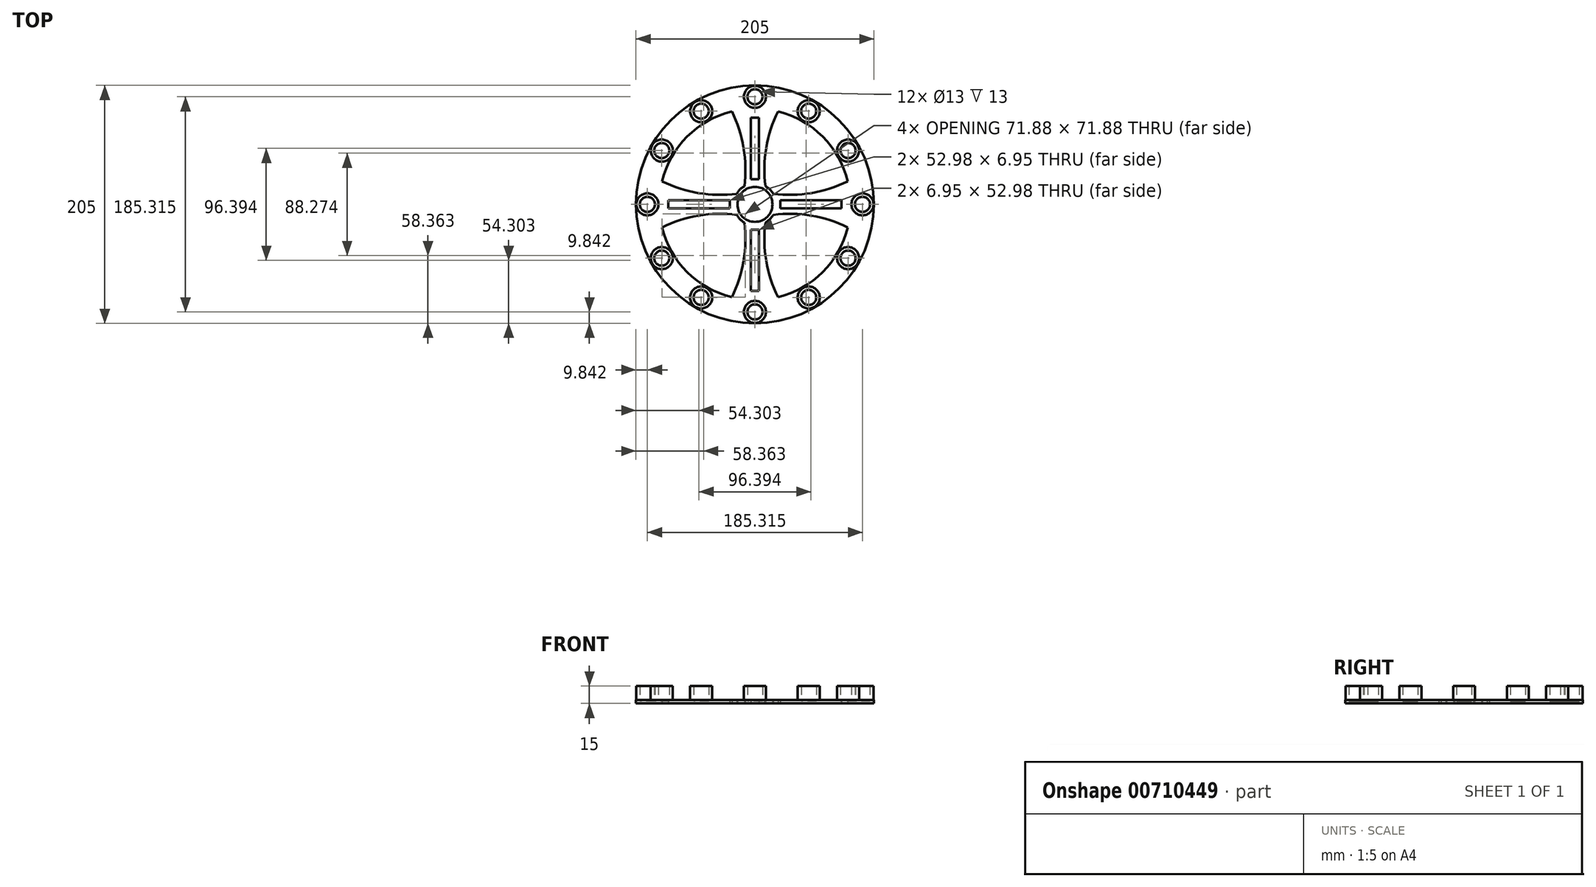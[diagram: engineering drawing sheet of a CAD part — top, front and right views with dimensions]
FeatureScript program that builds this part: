
annotation { "Feature Type Name" : "Feature", "Feature Type Description" : "" }
export const myFeature = defineFeature(function(context is Context, id is Id, definition is map)
    precondition{}
    {
        {
            var Q0;
            Q0=qCreatedBy(makeId("Top.planeOp"),FACE);
            var sketch = newSketch(context, id + "F0", { "sketchPlane" : qUnion([Q0])});
            skCircle(sketch, "E0", {"center": v(0, 0) * mm, "radius": 82.5 * mm});
            skCircle(sketch, "E1.0", {"center": v(0, 0) * mm, "radius": 102.5 * mm});
            skCircle(sketch, "E2", {"center": v(0, 92.66) * mm, "radius": 6.5 * mm});
            skCircle(sketch, "E3.0", {"center": v(0, 92.66) * mm, "radius": 9.5 * mm});
            skCircle(sketch, "E4.1.0", {"center": v(-46.33, 80.24) * mm, "radius": 9.5 * mm});
            skCircle(sketch, "E4.1.1", {"center": v(-46.33, 80.24) * mm, "radius": 6.5 * mm});
            skCircle(sketch, "E4.2.0", {"center": v(-80.24, 46.33) * mm, "radius": 9.5 * mm});
            skCircle(sketch, "E4.2.1", {"center": v(-80.24, 46.33) * mm, "radius": 6.5 * mm});
            skCircle(sketch, "E4.3.0", {"center": v(-92.66, 0) * mm, "radius": 9.5 * mm});
            skCircle(sketch, "E4.3.1", {"center": v(-92.66, 0) * mm, "radius": 6.5 * mm});
            skCircle(sketch, "E4.4.0", {"center": v(-80.24, -46.33) * mm, "radius": 9.5 * mm});
            skCircle(sketch, "E4.4.1", {"center": v(-80.24, -46.33) * mm, "radius": 6.5 * mm});
            skCircle(sketch, "E4.5.0", {"center": v(-46.33, -80.24) * mm, "radius": 9.5 * mm});
            skCircle(sketch, "E4.5.1", {"center": v(-46.33, -80.24) * mm, "radius": 6.5 * mm});
            skCircle(sketch, "E4.6.0", {"center": v(0, -92.66) * mm, "radius": 9.5 * mm});
            skCircle(sketch, "E4.6.1", {"center": v(0, -92.66) * mm, "radius": 6.5 * mm});
            skCircle(sketch, "E4.7.0", {"center": v(46.33, -80.24) * mm, "radius": 9.5 * mm});
            skCircle(sketch, "E4.7.1", {"center": v(46.33, -80.24) * mm, "radius": 6.5 * mm});
            skCircle(sketch, "E4.8.0", {"center": v(80.24, -46.33) * mm, "radius": 9.5 * mm});
            skCircle(sketch, "E4.8.1", {"center": v(80.24, -46.33) * mm, "radius": 6.5 * mm});
            skCircle(sketch, "E4.9.0", {"center": v(92.66, 0) * mm, "radius": 9.5 * mm});
            skCircle(sketch, "E4.9.1", {"center": v(92.66, 0) * mm, "radius": 6.5 * mm});
            skCircle(sketch, "E5.1.10.0", {"center": v(80.24, 46.33) * mm, "radius": 9.5 * mm});
            skCircle(sketch, "E5.2.10.0", {"center": v(80.24, 46.33) * mm, "radius": 6.5 * mm});
            skCircle(sketch, "E5.1.11.0", {"center": v(46.33, 80.24) * mm, "radius": 9.5 * mm});
            skCircle(sketch, "E5.2.11.0", {"center": v(46.33, 80.24) * mm, "radius": 6.5 * mm});
            skLineSegment(sketch, "E6.MirrorCS", {"start": v(-74.04, -3.28) * mm, "end": v(-74.04, 3.35) * mm});
            skArc(sketch, "E7", {"start": v(-80.07, 19.86) * mm, "mid": v(-46.62, 9.4) * mm, "end": v(-11.57, 9.7) * mm});
            skArc(sketch, "E8.1.0", {"start": v(-19.86, -80.07) * mm, "mid": v(-9.4, -46.62) * mm, "end": v(-9.7, -11.57) * mm});
            skArc(sketch, "E8.2.0", {"start": v(80.07, -19.86) * mm, "mid": v(46.62, -9.4) * mm, "end": v(11.57, -9.7) * mm});
            skArc(sketch, "E8.3.0", {"start": v(19.86, 80.07) * mm, "mid": v(9.4, 46.62) * mm, "end": v(9.7, 11.57) * mm});
            skArc(sketch, "E9.MirrorCS", {"start": v(-80.07, -19.86) * mm, "mid": v(-46.62, -9.4) * mm, "end": v(-11.57, -9.7) * mm});
            skArc(sketch, "E10.MirrorCS", {"start": v(19.86, -80.07) * mm, "mid": v(9.4, -46.62) * mm, "end": v(9.7, -11.57) * mm});
            skArc(sketch, "E11.MirrorCS", {"start": v(-19.86, 80.07) * mm, "mid": v(-9.4, 46.62) * mm, "end": v(-9.7, 11.57) * mm});
            skArc(sketch, "E12.MirrorCS", {"start": v(80.07, 19.86) * mm, "mid": v(46.62, 9.4) * mm, "end": v(11.57, 9.7) * mm});
            skLineSegment(sketch, "E13.bottom", {"start": v(-3.47, 74.69) * mm, "end": v(3.47, 74.69) * mm});
            skLineSegment(sketch, "E13.top", {"start": v(-3.47, 21.7) * mm, "end": v(3.47, 21.7) * mm});
            skLineSegment(sketch, "E13.left", {"start": v(-3.47, 74.69) * mm, "end": v(-3.47, 21.7) * mm});
            skLineSegment(sketch, "E13.right", {"start": v(3.47, 74.69) * mm, "end": v(3.47, 21.7) * mm});
            skPoint(sketch, "E13.middle", {"position": v(0, 48.2) * mm});
            skLineSegment(sketch, "E14.1.0", {"start": v(-74.69, 3.47) * mm, "end": v(-21.7, 3.47) * mm});
            skLineSegment(sketch, "E14.1.1", {"start": v(-74.69, -3.47) * mm, "end": v(-21.7, -3.47) * mm});
            skLineSegment(sketch, "E14.1.2", {"start": v(-74.69, -3.47) * mm, "end": v(-74.69, 3.47) * mm});
            skLineSegment(sketch, "E14.1.3", {"start": v(-21.7, -3.47) * mm, "end": v(-21.7, 3.47) * mm});
            skLineSegment(sketch, "E14.2.0", {"start": v(-3.47, -74.69) * mm, "end": v(-3.47, -21.7) * mm});
            skLineSegment(sketch, "E14.2.1", {"start": v(3.47, -74.69) * mm, "end": v(3.47, -21.7) * mm});
            skLineSegment(sketch, "E14.2.2", {"start": v(3.47, -74.69) * mm, "end": v(-3.47, -74.69) * mm});
            skLineSegment(sketch, "E14.2.3", {"start": v(3.47, -21.7) * mm, "end": v(-3.47, -21.7) * mm});
            skLineSegment(sketch, "E14.3.0", {"start": v(74.69, -3.47) * mm, "end": v(21.7, -3.47) * mm});
            skLineSegment(sketch, "E14.3.1", {"start": v(74.69, 3.47) * mm, "end": v(21.7, 3.47) * mm});
            skLineSegment(sketch, "E14.3.2", {"start": v(74.69, 3.47) * mm, "end": v(74.69, -3.47) * mm});
            skLineSegment(sketch, "E14.3.3", {"start": v(21.7, 3.47) * mm, "end": v(21.7, -3.47) * mm});
            skCircle(sketch, "E15", {"center": v(0, 0) * mm, "radius": 18.16 * mm});
            skCircle(sketch, "E16", {"center": v(0, 0) * mm, "radius": 15.1 * mm});
            skSolve(sketch);
        }
        {
            var Q0;
            Q0 = qSketchRegion(id + "F0", true);
            var Q1;
            Q1=makeQuery(id+"F0.imprint","IMPRINT",FACE,{"disambiguationData":[TD([[makeQuery(id+"F0.imprint","IMPRINT",EDGE,{"derivedFrom":sQuery(id+"F0.wireOp",EDGE,"E14.1.0")}),1.0]])]});
            var Q2;
            {var subQ0=sQuery(id+"F0.wireOp",EDGE,"E16");var subQ1=sQuery(id+"F0.wireOp",EDGE,"E7");var subQ2=makeQuery(id+"F0.imprint","INTERSECT",VERTEX,{"derivedFrom":[subQ1,subQ0]});Q2=makeQuery(id+"F0.imprint","IMPRINT",FACE,{"disambiguationData":[TD([[makeQuery(id+"F0.imprint","IMPRINT",EDGE,{"disambiguationData":[TD([[subQ2,1.0]])],"derivedFrom":subQ1}),-1.0]])]});}
            var Q3;
            {var subQ0=sQuery(id+"F0.wireOp",EDGE,"E16");var subQ1=sQuery(id+"F0.wireOp",EDGE,"E7");var subQ2=makeQuery(id+"F0.imprint","INTERSECT",VERTEX,{"derivedFrom":[subQ1,subQ0]});Q3=makeQuery(id+"F0.imprint","IMPRINT",FACE,{"disambiguationData":[TD([[makeQuery(id+"F0.imprint","IMPRINT",EDGE,{"disambiguationData":[TD([[subQ2,1.0]])],"derivedFrom":subQ1}),1.0]])]});}
            var Q4;
            {var subQ0=sQuery(id+"F0.wireOp",EDGE,"E16");var subQ1=sQuery(id+"F0.wireOp",EDGE,"E8.3.0");var subQ2=makeQuery(id+"F0.imprint","INTERSECT",VERTEX,{"derivedFrom":[subQ1,subQ0]});Q4=makeQuery(id+"F0.imprint","IMPRINT",FACE,{"disambiguationData":[TD([[makeQuery(id+"F0.imprint","IMPRINT",EDGE,{"disambiguationData":[TD([[subQ2,1.0]])],"derivedFrom":subQ1}),-1.0]])]});}
            var Q5;
            {var subQ0=sQuery(id+"F0.wireOp",EDGE,"E16");var subQ1=sQuery(id+"F0.wireOp",EDGE,"E8.3.0");var subQ2=makeQuery(id+"F0.imprint","INTERSECT",VERTEX,{"derivedFrom":[subQ1,subQ0]});Q5=makeQuery(id+"F0.imprint","IMPRINT",FACE,{"disambiguationData":[TD([[makeQuery(id+"F0.imprint","IMPRINT",EDGE,{"disambiguationData":[TD([[subQ2,1.0]])],"derivedFrom":subQ1}),1.0]])]});}
            var Q6;
            {var subQ0=sQuery(id+"F0.wireOp",EDGE,"E16");var subQ1=sQuery(id+"F0.wireOp",EDGE,"E8.2.0");var subQ2=makeQuery(id+"F0.imprint","INTERSECT",VERTEX,{"derivedFrom":[subQ1,subQ0]});Q6=makeQuery(id+"F0.imprint","IMPRINT",FACE,{"disambiguationData":[TD([[makeQuery(id+"F0.imprint","IMPRINT",EDGE,{"disambiguationData":[TD([[subQ2,1.0]])],"derivedFrom":subQ1}),-1.0]])]});}
            var Q7;
            Q7=makeQuery(id+"F0.imprint","IMPRINT",FACE,{"disambiguationData":[TD([[makeQuery(id+"F0.imprint","IMPRINT",EDGE,{"derivedFrom":sQuery(id+"F0.wireOp",EDGE,"E14.3.0")}),1.0]])]});
            var Q8;
            Q8=makeQuery(id+"F0.imprint","IMPRINT",FACE,{"disambiguationData":[TD([[makeQuery(id+"F0.imprint","IMPRINT",EDGE,{"derivedFrom":sQuery(id+"F0.wireOp",EDGE,"E14.2.0")}),1.0]])]});
            var Q9;
            {var subQ0=sQuery(id+"F0.wireOp",EDGE,"E16");var subQ1=sQuery(id+"F0.wireOp",EDGE,"E8.1.0");var subQ2=makeQuery(id+"F0.imprint","INTERSECT",VERTEX,{"derivedFrom":[subQ1,subQ0]});Q9=makeQuery(id+"F0.imprint","IMPRINT",FACE,{"disambiguationData":[TD([[makeQuery(id+"F0.imprint","IMPRINT",EDGE,{"disambiguationData":[TD([[subQ2,1.0]])],"derivedFrom":subQ1}),-1.0]])]});}
            var Q10;
            {var subQ0=sQuery(id+"F0.wireOp",EDGE,"E16");var subQ1=sQuery(id+"F0.wireOp",EDGE,"E8.2.0");var subQ2=makeQuery(id+"F0.imprint","INTERSECT",VERTEX,{"derivedFrom":[subQ1,subQ0]});Q10=makeQuery(id+"F0.imprint","IMPRINT",FACE,{"disambiguationData":[TD([[makeQuery(id+"F0.imprint","IMPRINT",EDGE,{"disambiguationData":[TD([[subQ2,1.0]])],"derivedFrom":subQ1}),1.0]])]});}
            var Q11;
            {var subQ0=sQuery(id+"F0.wireOp",EDGE,"E16");var subQ1=sQuery(id+"F0.wireOp",EDGE,"E8.1.0");var subQ2=makeQuery(id+"F0.imprint","INTERSECT",VERTEX,{"derivedFrom":[subQ1,subQ0]});Q11=makeQuery(id+"F0.imprint","IMPRINT",FACE,{"disambiguationData":[TD([[makeQuery(id+"F0.imprint","IMPRINT",EDGE,{"disambiguationData":[TD([[subQ2,1.0]])],"derivedFrom":subQ1}),1.0]])]});}
            var Q12;
            Q12=makeQuery(id+"F0.imprint","IMPRINT",FACE,{"disambiguationData":[TD([[makeQuery(id+"F0.imprint","IMPRINT",EDGE,{"derivedFrom":sQuery(id+"F0.wireOp",EDGE,"E13.bottom")}),1.0]])]});
            extrude(context, id + "F1", {"entities" : qUnion([Q0, Q1, Q2, Q3, Q4, Q5, Q6, Q7, Q8, Q9, Q10, Q11, Q12]), "depth" : 3 * mm, "offsetDistance" : 25 * mm});
        }
        {
            var Q0;
            Q0=makeQuery(id+"F0.imprint","IMPRINT",FACE,{"disambiguationData":[TD([[makeQuery(id+"F0.imprint","IMPRINT",EDGE,{"derivedFrom":sQuery(id+"F0.wireOp",EDGE,"E5.1.10.0")}),1.0]])]});
            var Q1;
            Q1=makeQuery(id+"F0.imprint","IMPRINT",FACE,{"disambiguationData":[TD([[makeQuery(id+"F0.imprint","IMPRINT",EDGE,{"derivedFrom":sQuery(id+"F0.wireOp",EDGE,"E4.9.0")}),1.0]])]});
            var Q2;
            Q2=makeQuery(id+"F0.imprint","IMPRINT",FACE,{"disambiguationData":[TD([[makeQuery(id+"F0.imprint","IMPRINT",EDGE,{"derivedFrom":sQuery(id+"F0.wireOp",EDGE,"E4.8.0")}),1.0]])]});
            var Q3;
            Q3=makeQuery(id+"F0.imprint","IMPRINT",FACE,{"disambiguationData":[TD([[makeQuery(id+"F0.imprint","IMPRINT",EDGE,{"derivedFrom":sQuery(id+"F0.wireOp",EDGE,"E4.7.0")}),1.0]])]});
            var Q4;
            Q4=makeQuery(id+"F0.imprint","IMPRINT",FACE,{"disambiguationData":[TD([[makeQuery(id+"F0.imprint","IMPRINT",EDGE,{"derivedFrom":sQuery(id+"F0.wireOp",EDGE,"E4.6.0")}),1.0]])]});
            var Q5;
            Q5=makeQuery(id+"F0.imprint","IMPRINT",FACE,{"disambiguationData":[TD([[makeQuery(id+"F0.imprint","IMPRINT",EDGE,{"derivedFrom":sQuery(id+"F0.wireOp",EDGE,"E4.5.0")}),1.0]])]});
            var Q6;
            Q6=makeQuery(id+"F0.imprint","IMPRINT",FACE,{"disambiguationData":[TD([[makeQuery(id+"F0.imprint","IMPRINT",EDGE,{"derivedFrom":sQuery(id+"F0.wireOp",EDGE,"E4.4.0")}),1.0]])]});
            var Q7;
            Q7=makeQuery(id+"F0.imprint","IMPRINT",FACE,{"disambiguationData":[TD([[makeQuery(id+"F0.imprint","IMPRINT",EDGE,{"derivedFrom":sQuery(id+"F0.wireOp",EDGE,"E4.3.0")}),1.0]])]});
            var Q8;
            Q8=makeQuery(id+"F0.imprint","IMPRINT",FACE,{"disambiguationData":[TD([[makeQuery(id+"F0.imprint","IMPRINT",EDGE,{"derivedFrom":sQuery(id+"F0.wireOp",EDGE,"E4.2.0")}),1.0]])]});
            var Q9;
            Q9=makeQuery(id+"F0.imprint","IMPRINT",FACE,{"disambiguationData":[TD([[makeQuery(id+"F0.imprint","IMPRINT",EDGE,{"derivedFrom":sQuery(id+"F0.wireOp",EDGE,"E5.1.11.0")}),1.0]])]});
            var Q10;
            Q10=makeQuery(id+"F0.imprint","IMPRINT",FACE,{"disambiguationData":[TD([[makeQuery(id+"F0.imprint","IMPRINT",EDGE,{"derivedFrom":sQuery(id+"F0.wireOp",EDGE,"E2")}),-1.0]])]});
            var Q11;
            Q11=makeQuery(id+"F0.imprint","IMPRINT",FACE,{"disambiguationData":[TD([[makeQuery(id+"F0.imprint","IMPRINT",EDGE,{"derivedFrom":sQuery(id+"F0.wireOp",EDGE,"E4.1.0")}),1.0]])]});
            extrude(context, id + "F2", {"entities" : qUnion([Q0, Q1, Q2, Q3, Q4, Q5, Q6, Q7, Q8, Q9, Q10, Q11]), "operationType" : NewBodyOperationType.ADD, "depth" : 15 * mm, "offsetDistance" : 25 * mm});
        }
        {
            var Q0;
            Q0=makeQuery(id+"F0.imprint","IMPRINT",FACE,{"disambiguationData":[TD([[makeQuery(id+"F0.imprint","IMPRINT",EDGE,{"derivedFrom":sQuery(id+"F0.wireOp",EDGE,"E2")}),1.0]])]});
            var Q1;
            Q1=makeQuery(id+"F0.imprint","IMPRINT",FACE,{"disambiguationData":[TD([[makeQuery(id+"F0.imprint","IMPRINT",EDGE,{"derivedFrom":sQuery(id+"F0.wireOp",EDGE,"E5.2.11.0")}),1.0]])]});
            var Q2;
            Q2=makeQuery(id+"F0.imprint","IMPRINT",FACE,{"disambiguationData":[TD([[makeQuery(id+"F0.imprint","IMPRINT",EDGE,{"derivedFrom":sQuery(id+"F0.wireOp",EDGE,"E5.2.10.0")}),1.0]])]});
            var Q3;
            Q3=makeQuery(id+"F0.imprint","IMPRINT",FACE,{"disambiguationData":[TD([[makeQuery(id+"F0.imprint","IMPRINT",EDGE,{"derivedFrom":sQuery(id+"F0.wireOp",EDGE,"E4.9.1")}),1.0]])]});
            var Q4;
            Q4=makeQuery(id+"F0.imprint","IMPRINT",FACE,{"disambiguationData":[TD([[makeQuery(id+"F0.imprint","IMPRINT",EDGE,{"derivedFrom":sQuery(id+"F0.wireOp",EDGE,"E4.8.1")}),1.0]])]});
            var Q5;
            Q5=makeQuery(id+"F0.imprint","IMPRINT",FACE,{"disambiguationData":[TD([[makeQuery(id+"F0.imprint","IMPRINT",EDGE,{"derivedFrom":sQuery(id+"F0.wireOp",EDGE,"E4.7.1")}),1.0]])]});
            var Q6;
            Q6=makeQuery(id+"F0.imprint","IMPRINT",FACE,{"disambiguationData":[TD([[makeQuery(id+"F0.imprint","IMPRINT",EDGE,{"derivedFrom":sQuery(id+"F0.wireOp",EDGE,"E4.6.1")}),1.0]])]});
            var Q7;
            Q7=makeQuery(id+"F0.imprint","IMPRINT",FACE,{"disambiguationData":[TD([[makeQuery(id+"F0.imprint","IMPRINT",EDGE,{"derivedFrom":sQuery(id+"F0.wireOp",EDGE,"E4.5.1")}),1.0]])]});
            var Q8;
            Q8=makeQuery(id+"F0.imprint","IMPRINT",FACE,{"disambiguationData":[TD([[makeQuery(id+"F0.imprint","IMPRINT",EDGE,{"derivedFrom":sQuery(id+"F0.wireOp",EDGE,"E4.4.1")}),1.0]])]});
            var Q9;
            Q9=makeQuery(id+"F0.imprint","IMPRINT",FACE,{"disambiguationData":[TD([[makeQuery(id+"F0.imprint","IMPRINT",EDGE,{"derivedFrom":sQuery(id+"F0.wireOp",EDGE,"E4.3.1")}),1.0]])]});
            var Q10;
            Q10=makeQuery(id+"F0.imprint","IMPRINT",FACE,{"disambiguationData":[TD([[makeQuery(id+"F0.imprint","IMPRINT",EDGE,{"derivedFrom":sQuery(id+"F0.wireOp",EDGE,"E4.2.1")}),1.0]])]});
            var Q11;
            Q11=makeQuery(id+"F0.imprint","IMPRINT",FACE,{"disambiguationData":[TD([[makeQuery(id+"F0.imprint","IMPRINT",EDGE,{"derivedFrom":sQuery(id+"F0.wireOp",EDGE,"E4.1.1")}),1.0]])]});
            extrude(context, id + "F3", {"entities" : qUnion([Q0, Q1, Q2, Q3, Q4, Q5, Q6, Q7, Q8, Q9, Q10, Q11]), "operationType" : NewBodyOperationType.ADD, "depth" : 2 * mm, "offsetDistance" : 25 * mm});
        }
    });
